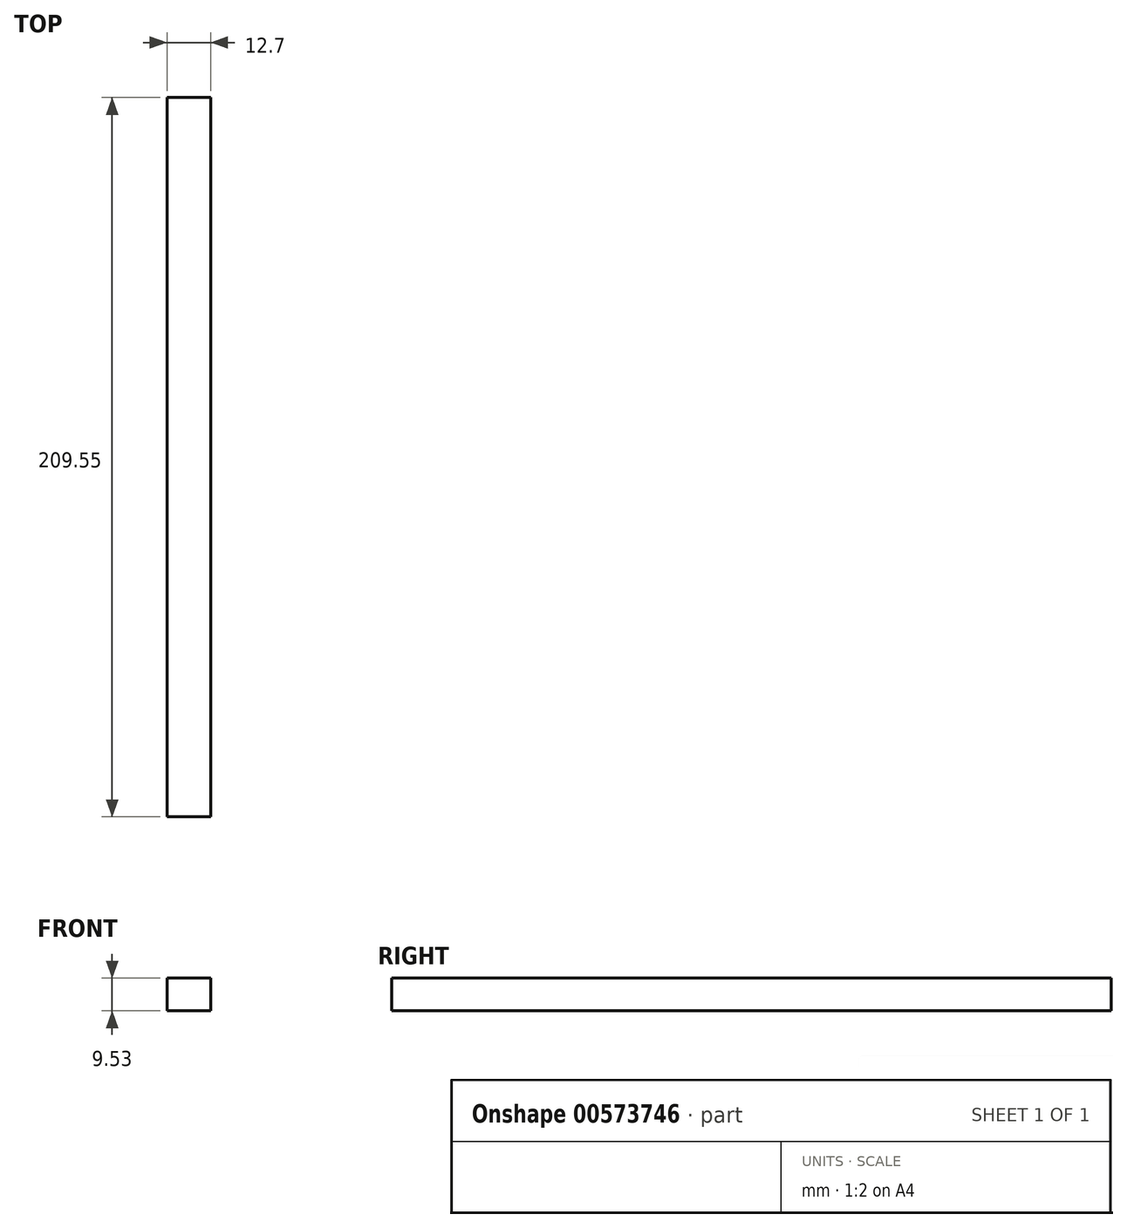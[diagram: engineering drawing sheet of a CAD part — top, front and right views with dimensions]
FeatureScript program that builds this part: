
annotation { "Feature Type Name" : "Feature", "Feature Type Description" : "" }
export const myFeature = defineFeature(function(context is Context, id is Id, definition is map)
    precondition{}
    {
        {
            var Q0;
            Q0=qCreatedBy(makeId("Top.planeOp"),FACE);
            var sketch = newSketch(context, id + "F0", { "sketchPlane" : qUnion([Q0])});
            skLineSegment(sketch, "E0.bottom", {"start": v(0, 0) * mm, "end": v(12.7, 0) * mm});
            skLineSegment(sketch, "E0.top", {"start": v(0, -209.55) * mm, "end": v(12.7, -209.55) * mm});
            skLineSegment(sketch, "E0.left", {"start": v(0, 0) * mm, "end": v(0, -209.55) * mm});
            skLineSegment(sketch, "E0.right", {"start": v(12.7, 0) * mm, "end": v(12.7, -209.55) * mm});
            skSolve(sketch);
        }
        {
            var Q0;
            Q0=makeQuery(id+"F0.imprint","IMPRINT",FACE,{"disambiguationData":[TD([[makeQuery(id+"F0.imprint","IMPRINT",EDGE,{"derivedFrom":sQuery(id+"F0.wireOp",EDGE,"E0.bottom")}),-1.0]])]});
            extrude(context, id + "F1", {"entities" : qUnion([Q0]), "depth" : 9.52 * mm, "offsetDistance" : 25.4 * mm});
        }
    });
